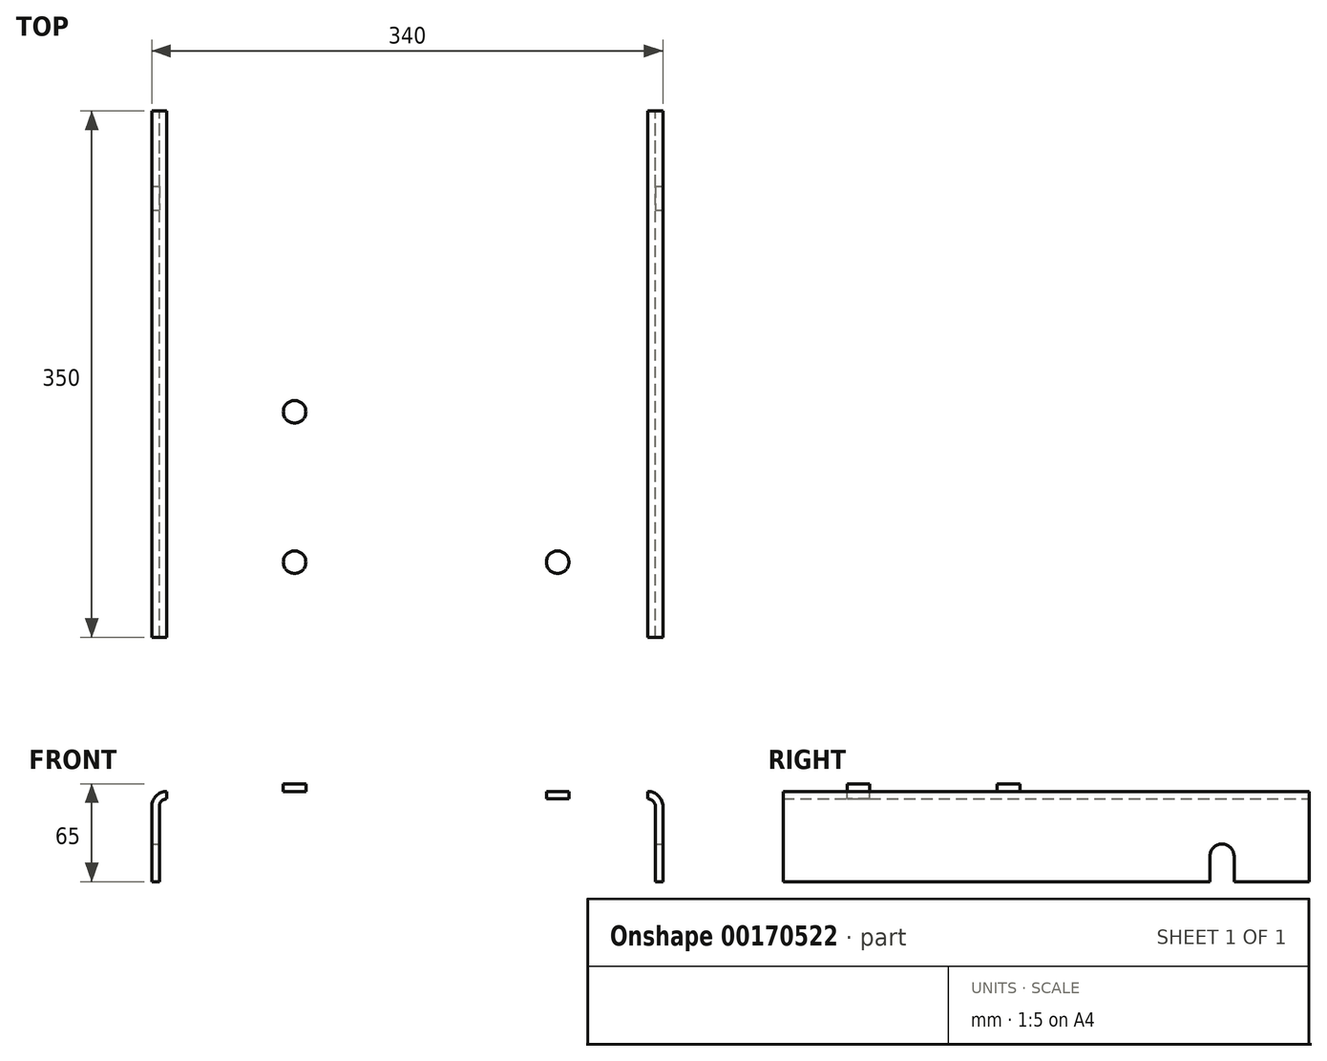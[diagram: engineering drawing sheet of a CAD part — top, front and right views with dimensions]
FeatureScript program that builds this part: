
annotation { "Feature Type Name" : "Feature", "Feature Type Description" : "" }
export const myFeature = defineFeature(function(context is Context, id is Id, definition is map)
    precondition{}
    {
        {
            var Q0;
            Q0=qCreatedBy(makeId("Front.planeOp"),FACE);
            var sketch = newSketch(context, id + "F0", { "sketchPlane" : qUnion([Q0])});
            skLineSegment(sketch, "E0", {"start": v(-275.6, 0) * mm, "end": v(396.04, 0) * mm, "construction": true});
            skLineSegment(sketch, "E1", {"start": v(0, 289.56) * mm, "end": v(0, -312.82) * mm, "construction": true});
            skLineSegment(sketch, "E2.bottom", {"start": v(-160, -88.7) * mm, "end": v(160, -88.7) * mm});
            skLineSegment(sketch, "E2.top", {"start": v(-170, -148.7) * mm, "end": v(-165, -148.7) * mm});
            skLineSegment(sketch, "E2.left", {"start": v(-170, -98.7) * mm, "end": v(-170, -148.7) * mm});
            skLineSegment(sketch, "E2.right", {"start": v(170, -98.7) * mm, "end": v(170, -148.7) * mm});
            skLineSegment(sketch, "E3.0", {"start": v(-165, -98.7) * mm, "end": v(-165, -148.7) * mm});
            skLineSegment(sketch, "E4.0", {"start": v(165, -98.7) * mm, "end": v(165, -148.7) * mm});
            skLineSegment(sketch, "E5.0", {"start": v(-160, -93.7) * mm, "end": v(160, -93.7) * mm});
            skArc(sketch, "E6.filletArc", {"start": v(-160, -93.7) * mm, "mid": v(-163.54, -95.16) * mm, "end": v(-165, -98.7) * mm});
            skArc(sketch, "E7.filletArc", {"start": v(165, -98.7) * mm, "mid": v(163.54, -95.16) * mm, "end": v(160, -93.7) * mm});
            skArc(sketch, "E8.0", {"start": v(170, -98.7) * mm, "mid": v(167.07, -91.63) * mm, "end": v(160, -88.7) * mm});
            skArc(sketch, "E9.0", {"start": v(-160, -88.7) * mm, "mid": v(-167.07, -91.63) * mm, "end": v(-170, -98.7) * mm});
            skLineSegment(sketch, "E10.trimOffspring", {"start": v(165, -148.7) * mm, "end": v(170, -148.7) * mm});
            skSolve(sketch);
        }
        {
            var Q0;
            Q0=makeQuery(id+"F0.imprint","IMPRINT",FACE,{"disambiguationData":[TD([[makeQuery(id+"F0.imprint","IMPRINT",EDGE,{"derivedFrom":sQuery(id+"F0.wireOp",EDGE,"E2.bottom")}),-1.0]])]});
            extrude(context, id + "F1", {"entities" : qUnion([Q0]), "depth" : 350 * mm});
        }
        {
            var Q0;
            Q0=makeQuery(id+"F1.opExtrude","SWEPT_FACE",FACE,{"disambiguationData":[OSD([sQuery(id+"F0.wireOp",EDGE,"E2.right")])]});
            var sketch = newSketch(context, id + "F2", { "sketchPlane" : qUnion([Q0])});
            skLineSegment(sketch, "E11", {"start": v(-238.25, -148.7) * mm, "end": v(14.74, -148.7) * mm, "construction": true});
            skLineSegment(sketch, "E12", {"start": v(0, -35.62) * mm, "end": v(0, -159.72) * mm, "construction": true});
            skLineSegment(sketch, "E13.bottom", {"start": v(-50, -148.7) * mm, "end": v(-66, -148.7) * mm});
            skLineSegment(sketch, "E13.top", {"start": v(-58, -123.7) * mm, "end": v(-58, -123.7) * mm});
            skLineSegment(sketch, "E13.left", {"start": v(-50, -148.7) * mm, "end": v(-50, -131.7) * mm});
            skLineSegment(sketch, "E13.right", {"start": v(-66, -148.7) * mm, "end": v(-66, -131.7) * mm});
            skPoint(sketch, "E14.visualSharp", {"position": v(-66, -123.7) * mm});
            skArc(sketch, "E14.filletArc", {"start": v(-58, -123.7) * mm, "mid": v(-63.66, -126.04) * mm, "end": v(-66, -131.7) * mm});
            skPoint(sketch, "E15.visualSharp", {"position": v(-50, -123.7) * mm});
            skArc(sketch, "E15.filletArc", {"start": v(-50, -131.7) * mm, "mid": v(-52.34, -126.04) * mm, "end": v(-58, -123.7) * mm});
            skSolve(sketch);
        }
        {
            var Q0;
            Q0=makeQuery(id+"F2.imprint","IMPRINT",FACE,{"disambiguationData":[TD([[makeQuery(id+"F2.imprint","IMPRINT",EDGE,{"derivedFrom":sQuery(id+"F2.wireOp",EDGE,"E13.bottom")}),1.0]])]});
            extrude(context, id + "F3", {"entities" : qUnion([Q0]), "operationType" : NewBodyOperationType.REMOVE, "endBound" : BoundingType.THROUGH_ALL, "oppositeDirection" : true, "depth" : 25 * mm});
        }
        {
            var Q0;
            Q0=makeQuery(id+"F1.opExtrude","SWEPT_FACE",FACE,{"disambiguationData":[OSD([sQuery(id+"F0.wireOp",EDGE,"E2.bottom")])]});
            var sketch = newSketch(context, id + "F4", { "sketchPlane" : qUnion([Q0])});
            skLineSegment(sketch, "E16", {"start": v(0, 0) * mm, "end": v(0, -142.57) * mm, "construction": true});
            skCircle(sketch, "E17", {"center": v(-100, -300) * mm, "radius": 7.5 * mm});
            skLineSegment(sketch, "E18", {"start": v(-160, 0) * mm, "end": v(160, 0) * mm, "construction": true});
            skCircle(sketch, "E19.MirrorC", {"center": v(100, -300) * mm, "radius": 7.5 * mm});
            skSolve(sketch);
        }
        {
            var Q0;
            Q0=makeQuery(id+"F4.imprint","IMPRINT",FACE,{"disambiguationData":[TD([[makeQuery(id+"F4.imprint","IMPRINT",EDGE,{"derivedFrom":sQuery(id+"F4.wireOp",EDGE,"E17")}),1.0]])]});
            var Q1;
            Q1=makeQuery(id+"F4.imprint","IMPRINT",FACE,{"disambiguationData":[TD([[makeQuery(id+"F4.imprint","IMPRINT",EDGE,{"derivedFrom":sQuery(id+"F4.wireOp",EDGE,"E19.MirrorC")}),-1.0]])]});
            extrude(context, id + "F5", {"entities" : qUnion([Q0, Q1]), "operationType" : NewBodyOperationType.REMOVE, "endBound" : BoundingType.UP_TO_NEXT, "oppositeDirection" : true, "depth" : 25 * mm});
        }
        {
            var Q0;
            Q0=makeQuery(id+"F1.opExtrude","SWEPT_FACE",FACE,{"disambiguationData":[OSD([sQuery(id+"F0.wireOp",EDGE,"E2.bottom")])]});
            var sketch = newSketch(context, id + "F6", { "sketchPlane" : qUnion([Q0])});
            skCircle(sketch, "E20", {"center": v(-75, -200) * mm, "radius": 7.5 * mm});
            skCircle(sketch, "E21", {"center": v(-75, -300) * mm, "radius": 7.5 * mm});
            skLineSegment(sketch, "E22", {"start": v(0, 0) * mm, "end": v(0, -382.25) * mm, "construction": true});
            skPoint(sketch, "E22.endSnap0", {"position": v(0, -350) * mm});
            skCircle(sketch, "E23.MirrorC", {"center": v(75, -300) * mm, "radius": 7.5 * mm});
            skCircle(sketch, "E24.MirrorC", {"center": v(75, -200) * mm, "radius": 7.5 * mm});
            skSolve(sketch);
        }
        {
            var Q0;
            Q0=makeQuery(id+"F6.imprint","IMPRINT",FACE,{"disambiguationData":[TD([[makeQuery(id+"F6.imprint","IMPRINT",EDGE,{"derivedFrom":sQuery(id+"F6.wireOp",EDGE,"E20")}),1.0]])]});
            var Q1;
            Q1=makeQuery(id+"F6.imprint","IMPRINT",FACE,{"disambiguationData":[TD([[makeQuery(id+"F6.imprint","IMPRINT",EDGE,{"derivedFrom":sQuery(id+"F6.wireOp",EDGE,"E21")}),1.0]])]});
            var Q2;
            Q2=makeQuery(id+"F6.imprint","IMPRINT",FACE,{"disambiguationData":[TD([[makeQuery(id+"F6.imprint","IMPRINT",EDGE,{"derivedFrom":sQuery(id+"F6.wireOp",EDGE,"E23.MirrorC")}),-1.0]])]});
            var Q3;
            Q3=makeQuery(id+"F6.imprint","IMPRINT",FACE,{"disambiguationData":[TD([[makeQuery(id+"F6.imprint","IMPRINT",EDGE,{"derivedFrom":sQuery(id+"F6.wireOp",EDGE,"E24.MirrorC")}),-1.0]])]});
            extrude(context, id + "F7", {"entities" : qUnion([Q0, Q1, Q2, Q3]), "operationType" : NewBodyOperationType.ADD, "depth" : 5 * mm});
        }
    });
